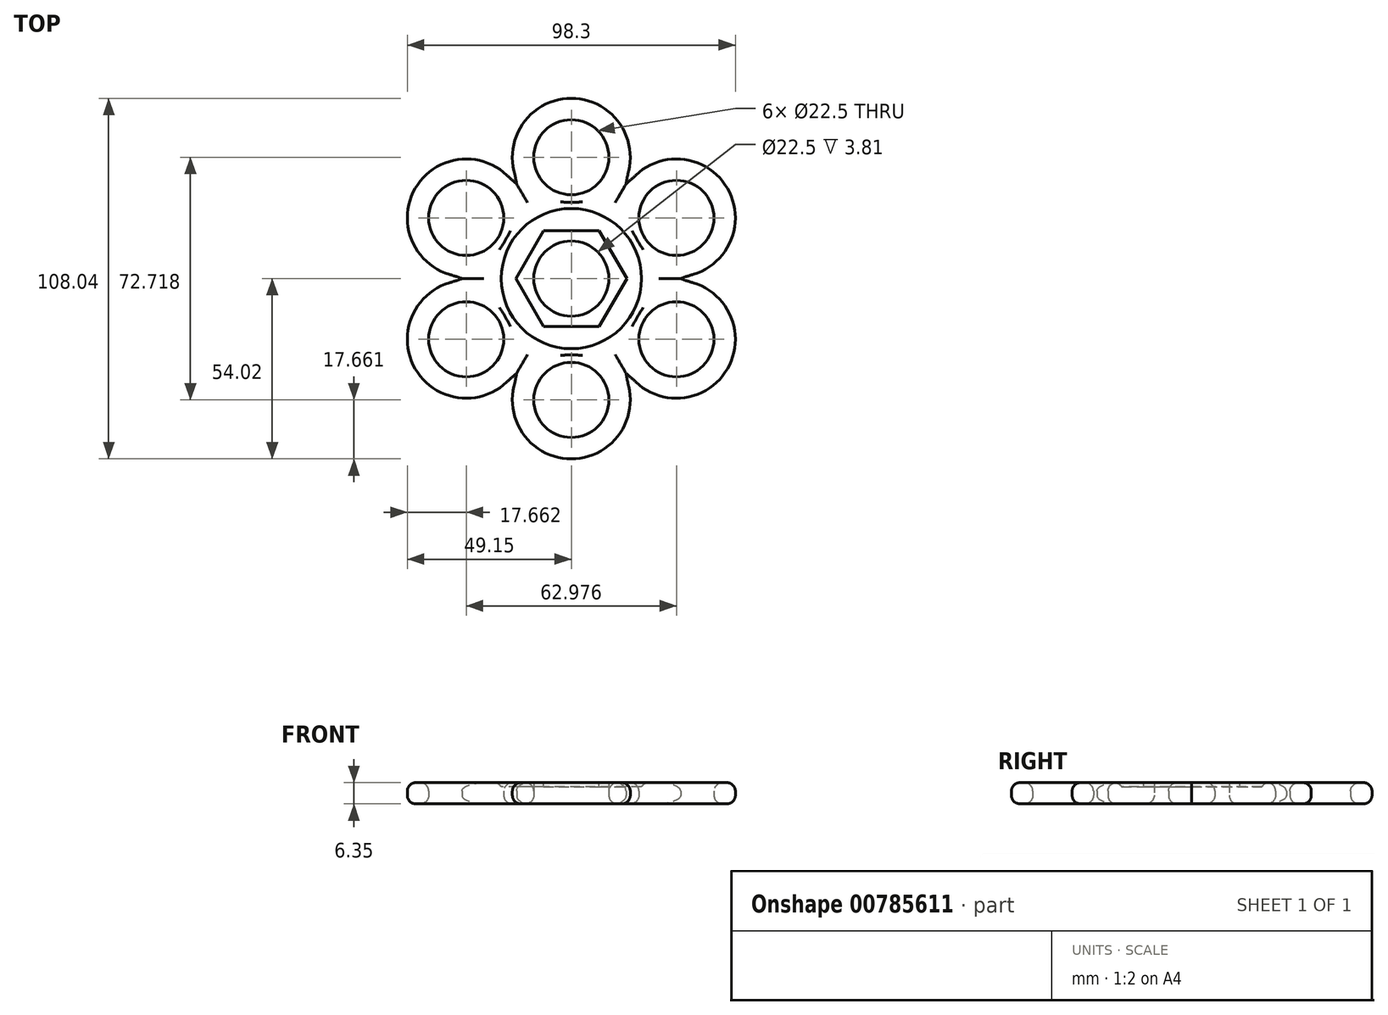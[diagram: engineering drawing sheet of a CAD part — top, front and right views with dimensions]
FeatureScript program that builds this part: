
annotation { "Feature Type Name" : "Feature", "Feature Type Description" : "" }
export const myFeature = defineFeature(function(context is Context, id is Id, definition is map)
    precondition{}
    {
        {
            var Q0;
            Q0=qCreatedBy(makeId("Top.planeOp"),FACE);
            var sketch = newSketch(context, id + "F0", { "sketchPlane" : qUnion([Q0])});
            skCircle(sketch, "E0", {"center": v(0, 0) * mm, "radius": 11.25 * mm});
            skCircle(sketch, "E1", {"center": v(0, 36.36) * mm, "radius": 11.25 * mm});
            skArc(sketch, "E2", {"start": v(17.17, 32.24) * mm, "mid": v(0, 54.02) * mm, "end": v(-17.17, 32.24) * mm});
            skArc(sketch, "E3", {"start": v(-17.17, 4.12) * mm, "mid": v(0, -17.66) * mm, "end": v(17.17, 4.12) * mm});
            skArc(sketch, "E4", {"start": v(-17.17, 4.12) * mm, "mid": v(-15.51, 18.18) * mm, "end": v(-17.17, 32.24) * mm});
            skArc(sketch, "E5", {"start": v(17.17, 32.24) * mm, "mid": v(15.51, 18.18) * mm, "end": v(17.17, 4.12) * mm});
            skSolve(sketch);
        }
        {
            var Q0;
            Q0=makeQuery(id+"F0.imprint","IMPRINT",FACE,{"disambiguationData":[TD([[makeQuery(id+"F0.imprint","IMPRINT",EDGE,{"derivedFrom":sQuery(id+"F0.wireOp",EDGE,"E0")}),-1.0]])]});
            extrude(context, id + "F1", {"entities" : qUnion([Q0]), "depth" : 6.35 * mm, "offsetDistance" : 25.4 * mm});
        }
        {
            var Q0;
            Q0=makeQuery(id+"F1.opExtrude","SWEPT_BODY",BODY,{"disambiguationData":[OSD([sQuery(id+"F0.wireOp",EDGE,"E0"),sQuery(id+"F0.wireOp",EDGE,"E1"),sQuery(id+"F0.wireOp",EDGE,"E2"),sQuery(id+"F0.wireOp",EDGE,"E3"),sQuery(id+"F0.wireOp",EDGE,"E4"),sQuery(id+"F0.wireOp",EDGE,"E5")])]});
            var Q1;
            Q1=sQuery(id+"F0.wireOp",EDGE,"E0");
            circularPattern(context, id + "F2", {"operationType" : NewBodyOperationType.ADD, "entities" : qUnion([Q0]), "axis" : qUnion([Q1]), "angle" : 360 * degree, "instanceCount" : 6, "equalSpace" : true});
        }
        {
            var Q0;
            {var subQ0=makeQuery(id+"F1.opExtrude","CAP_FACE",FACE,{"disambiguationData":[OSD([sQuery(id+"F0.wireOp",EDGE,"E0"),sQuery(id+"F0.wireOp",EDGE,"E1"),sQuery(id+"F0.wireOp",EDGE,"E2"),sQuery(id+"F0.wireOp",EDGE,"E3"),sQuery(id+"F0.wireOp",EDGE,"E4"),sQuery(id+"F0.wireOp",EDGE,"E5")])],"isStart":false});Q0=makeQuery(id+"F2.boolean.opBoolean","MERGE",FACE,{"derivedFrom":[subQ0,makeQuery(id+"F2.opPattern","COPY",FACE,{"derivedFrom":subQ0,"instanceName":"1"}),makeQuery(id+"F2.opPattern","COPY",FACE,{"derivedFrom":subQ0,"instanceName":"2"}),makeQuery(id+"F2.opPattern","COPY",FACE,{"derivedFrom":subQ0,"instanceName":"3"}),makeQuery(id+"F2.opPattern","COPY",FACE,{"derivedFrom":subQ0,"instanceName":"4"}),makeQuery(id+"F2.opPattern","COPY",FACE,{"derivedFrom":subQ0,"instanceName":"5"})]});}
            var sketch = newSketch(context, id + "F3", { "sketchPlane" : qUnion([Q0])});
            skCircle(sketch, "E6.cCircle", {"center": v(0, 0) * mm, "radius": 14.4 * mm, "construction": true});
            skLineSegment(sketch, "E6.0", {"start": v(-16.63, 0) * mm, "end": v(-8.32, 14.4) * mm});
            skLineSegment(sketch, "E6.1", {"start": v(-8.32, 14.4) * mm, "end": v(8.32, 14.4) * mm});
            skLineSegment(sketch, "E6.2", {"start": v(8.32, 14.4) * mm, "end": v(16.63, 0) * mm});
            skLineSegment(sketch, "E6.3", {"start": v(16.63, 0) * mm, "end": v(8.32, -14.4) * mm});
            skLineSegment(sketch, "E6.4", {"start": v(8.32, -14.4) * mm, "end": v(-8.32, -14.4) * mm});
            skLineSegment(sketch, "E6.5", {"start": v(-8.32, -14.4) * mm, "end": v(-16.63, 0) * mm});
            skPoint(sketch, "E6.0.midPoint", {"position": v(-12.47, 7.2) * mm});
            skCircle(sketch, "E7", {"center": v(0, 0) * mm, "radius": 21 * mm});
            skSolve(sketch);
        }
        {
            var Q0;
            Q0=makeQuery(id+"F3.imprint","IMPRINT",FACE,{"disambiguationData":[TD([[makeQuery(id+"F3.imprint","IMPRINT",EDGE,{"derivedFrom":sQuery(id+"F3.wireOp",EDGE,"E6.0")}),1.0]])]});
            extrude(context, id + "F4", {"entities" : qUnion([Q0]), "operationType" : NewBodyOperationType.REMOVE, "oppositeDirection" : true, "depth" : 1.27 * mm, "offsetDistance" : 25.4 * mm});
        }
        {
            var Q0;
            Q0=makeQuery(id+"F2.opPattern","COPY",EDGE,{"derivedFrom":makeQuery(id+"F1.opExtrude","CAP_EDGE",EDGE,{"disambiguationData":[OSD([sQuery(id+"F0.wireOp",EDGE,"E2")])],"isStart":false}),"instanceName":"1"});
            var Q1;
            Q1=makeQuery(id+"F2.opPattern","COPY",EDGE,{"derivedFrom":makeQuery(id+"F1.opExtrude","CAP_EDGE",EDGE,{"disambiguationData":[OSD([sQuery(id+"F0.wireOp",EDGE,"E2")])],"isStart":false}),"instanceName":"2"});
            var Q2;
            Q2=makeQuery(id+"F2.opPattern","COPY",EDGE,{"derivedFrom":makeQuery(id+"F1.opExtrude","CAP_EDGE",EDGE,{"disambiguationData":[OSD([sQuery(id+"F0.wireOp",EDGE,"E2")])],"isStart":true}),"instanceName":"3"});
            var Q3;
            {var subQ0=sQuery(id+"F0.wireOp",EDGE,"E2");var subQ2=sQuery(id+"F0.wireOp",EDGE,"E5");var subQ4=sQuery(id+"F0.wireOp",EDGE,"E4");var subQ6=sQuery(id+"F0.wireOp",EDGE,"E1");var subQ7=makeQuery(id+"F1.opExtrude","SWEPT_FACE",FACE,{"disambiguationData":[OSD([subQ6])]});var subQ8=makeQuery(id+"F1.opExtrude","CAP_FACE",FACE,{"disambiguationData":[OSD([sQuery(id+"F0.wireOp",EDGE,"E0"),subQ6,subQ0,sQuery(id+"F0.wireOp",EDGE,"E3"),subQ4,subQ2])],"isStart":false});Q3=makeQuery(id+"F4.boolean.opBoolean","SPLIT",FACE,{"disambiguationData":[TD([subQ7])],"derivedFrom":makeQuery(id+"F2.boolean.opBoolean","MERGE",FACE,{"derivedFrom":[subQ8,makeQuery(id+"F2.opPattern","COPY",FACE,{"derivedFrom":subQ8,"instanceName":"1"}),makeQuery(id+"F2.opPattern","COPY",FACE,{"derivedFrom":subQ8,"instanceName":"2"}),makeQuery(id+"F2.opPattern","COPY",FACE,{"derivedFrom":subQ8,"instanceName":"3"}),makeQuery(id+"F2.opPattern","COPY",FACE,{"derivedFrom":subQ8,"instanceName":"4"}),makeQuery(id+"F2.opPattern","COPY",FACE,{"derivedFrom":subQ8,"instanceName":"5"})]})});}
            var Q4;
            {var subQ0=makeQuery(id+"F1.opExtrude","CAP_FACE",FACE,{"disambiguationData":[OSD([sQuery(id+"F0.wireOp",EDGE,"E0"),sQuery(id+"F0.wireOp",EDGE,"E1"),sQuery(id+"F0.wireOp",EDGE,"E2"),sQuery(id+"F0.wireOp",EDGE,"E3"),sQuery(id+"F0.wireOp",EDGE,"E4"),sQuery(id+"F0.wireOp",EDGE,"E5")])],"isStart":true});Q4=makeQuery(id+"F2.boolean.opBoolean","MERGE",FACE,{"derivedFrom":[subQ0,makeQuery(id+"F2.opPattern","COPY",FACE,{"derivedFrom":subQ0,"instanceName":"1"}),makeQuery(id+"F2.opPattern","COPY",FACE,{"derivedFrom":subQ0,"instanceName":"2"}),makeQuery(id+"F2.opPattern","COPY",FACE,{"derivedFrom":subQ0,"instanceName":"3"}),makeQuery(id+"F2.opPattern","COPY",FACE,{"derivedFrom":subQ0,"instanceName":"4"}),makeQuery(id+"F2.opPattern","COPY",FACE,{"derivedFrom":subQ0,"instanceName":"5"})]});}
            fillet(context, id + "F5", {"entities" : qUnion([Q0, Q1, Q2, Q3, Q4]), "radius" : 2.54 * mm, "tangentPropagation" : true, "allowEdgeOverflow" : false});
        }
    });
